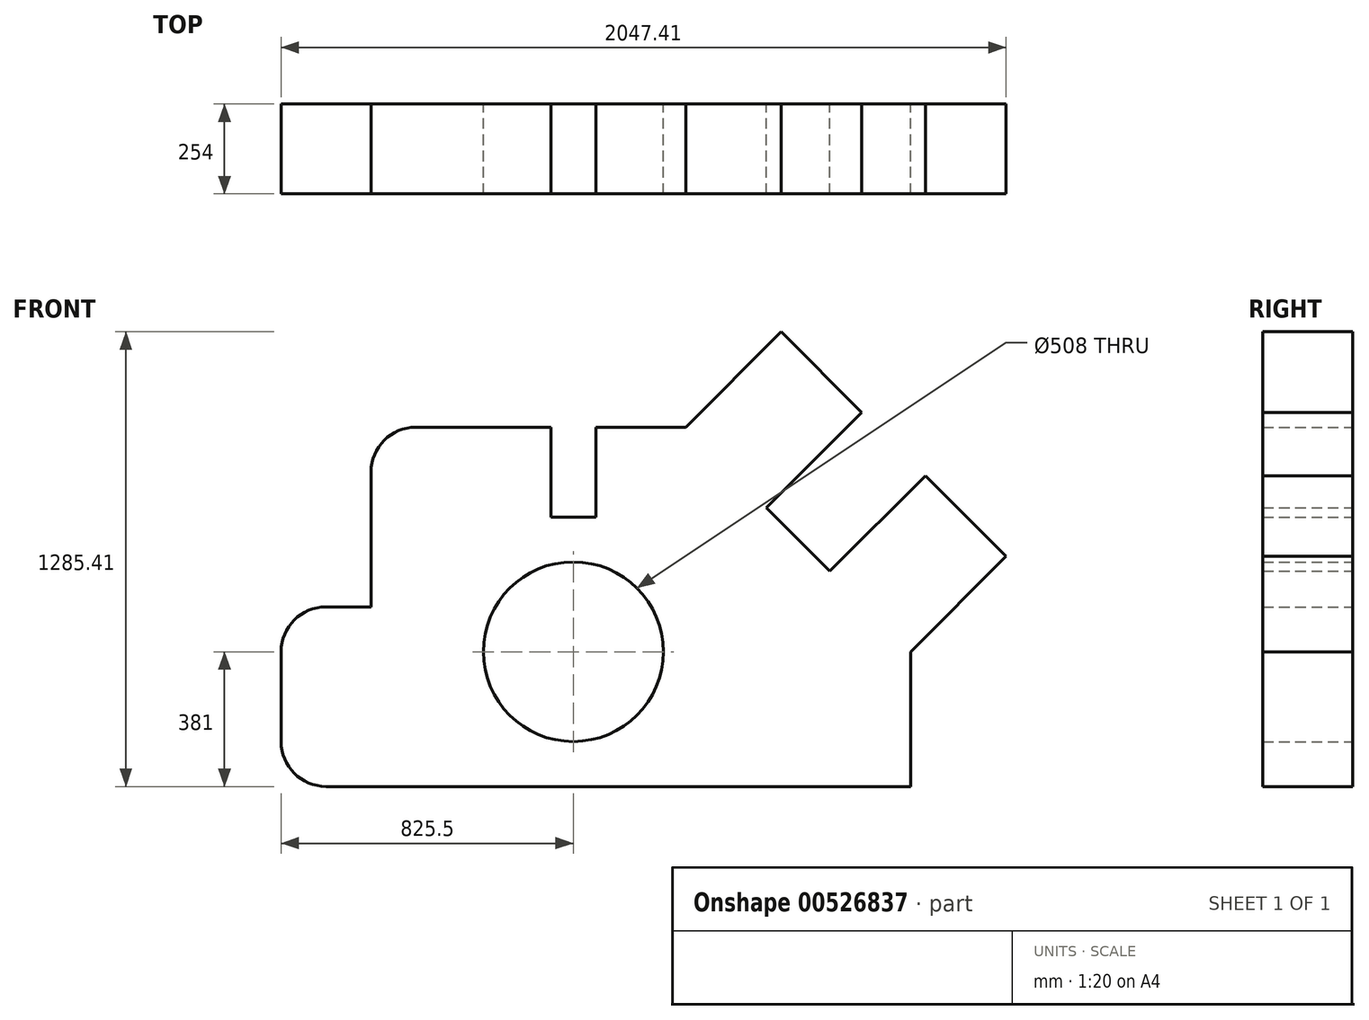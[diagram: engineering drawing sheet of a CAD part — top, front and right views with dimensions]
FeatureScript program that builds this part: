
annotation { "Feature Type Name" : "Feature", "Feature Type Description" : "" }
export const myFeature = defineFeature(function(context is Context, id is Id, definition is map)
    precondition{}
    {
        {
            var Q0;
            Q0=qCreatedBy(makeId("Front.planeOp"),FACE);
            var sketch = newSketch(context, id + "F0", { "sketchPlane" : qUnion([Q0])});
            skLineSegment(sketch, "E0", {"start": v(127, 0) * mm, "end": v(1778, 0) * mm});
            skLineSegment(sketch, "E1", {"start": v(1778, 0) * mm, "end": v(1778, 381) * mm});
            skLineSegment(sketch, "E2", {"start": v(0, 127) * mm, "end": v(0, 381) * mm});
            skPoint(sketch, "E3.visualSharp", {"position": v(0, 0) * mm});
            skArc(sketch, "E3.filletArc", {"start": v(0, 127) * mm, "mid": v(37.2, 37.2) * mm, "end": v(127, 0) * mm});
            skCircle(sketch, "E4", {"center": v(825.5, 381) * mm, "radius": 254 * mm});
            skLineSegment(sketch, "E5", {"start": v(127, 508) * mm, "end": v(254, 508) * mm});
            skLineSegment(sketch, "E6", {"start": v(254, 508) * mm, "end": v(254, 889) * mm});
            skLineSegment(sketch, "E7", {"start": v(381, 1016) * mm, "end": v(762, 1016) * mm});
            skLineSegment(sketch, "E8", {"start": v(762, 1016) * mm, "end": v(762, 762) * mm});
            skLineSegment(sketch, "E9", {"start": v(762, 762) * mm, "end": v(889, 762) * mm});
            skLineSegment(sketch, "E10", {"start": v(889, 762) * mm, "end": v(889, 1016) * mm});
            skLineSegment(sketch, "E11", {"start": v(889, 1016) * mm, "end": v(1143, 1016) * mm});
            skPoint(sketch, "E12.visualSharp", {"position": v(0, 508) * mm});
            skArc(sketch, "E12.filletArc", {"start": v(127, 508) * mm, "mid": v(37.2, 470.8) * mm, "end": v(0, 381) * mm});
            skPoint(sketch, "E13.visualSharp", {"position": v(254, 1016) * mm});
            skArc(sketch, "E13.filletArc", {"start": v(381, 1016) * mm, "mid": v(291.2, 978.8) * mm, "end": v(254, 889) * mm});
            skLineSegment(sketch, "E14", {"start": v(1778, 381) * mm, "end": v(2047.4, 650.4) * mm});
            skLineSegment(sketch, "E15", {"start": v(2047.4, 650.4) * mm, "end": v(1819.71, 878.1) * mm});
            skLineSegment(sketch, "E16", {"start": v(1819.71, 878.1) * mm, "end": v(1550.3, 608.7) * mm});
            skLineSegment(sketch, "E17", {"start": v(1550.3, 608.7) * mm, "end": v(1370.7, 788.3) * mm});
            skLineSegment(sketch, "E18", {"start": v(1370.7, 788.3) * mm, "end": v(1640.1, 1057.71) * mm});
            skLineSegment(sketch, "E19", {"start": v(1412.4, 1285.4) * mm, "end": v(1143, 1016) * mm});
            skLineSegment(sketch, "E20", {"start": v(1640.1, 1057.71) * mm, "end": v(1412.4, 1285.4) * mm});
            skSolve(sketch);
        }
        {
            var Q0;
            Q0 = qSketchRegion(id + "F0", true);
            extrude(context, id + "F1", {"entities" : qUnion([Q0]), "depth" : 254 * mm, "offsetDistance" : 25.4 * mm});
        }
    });
